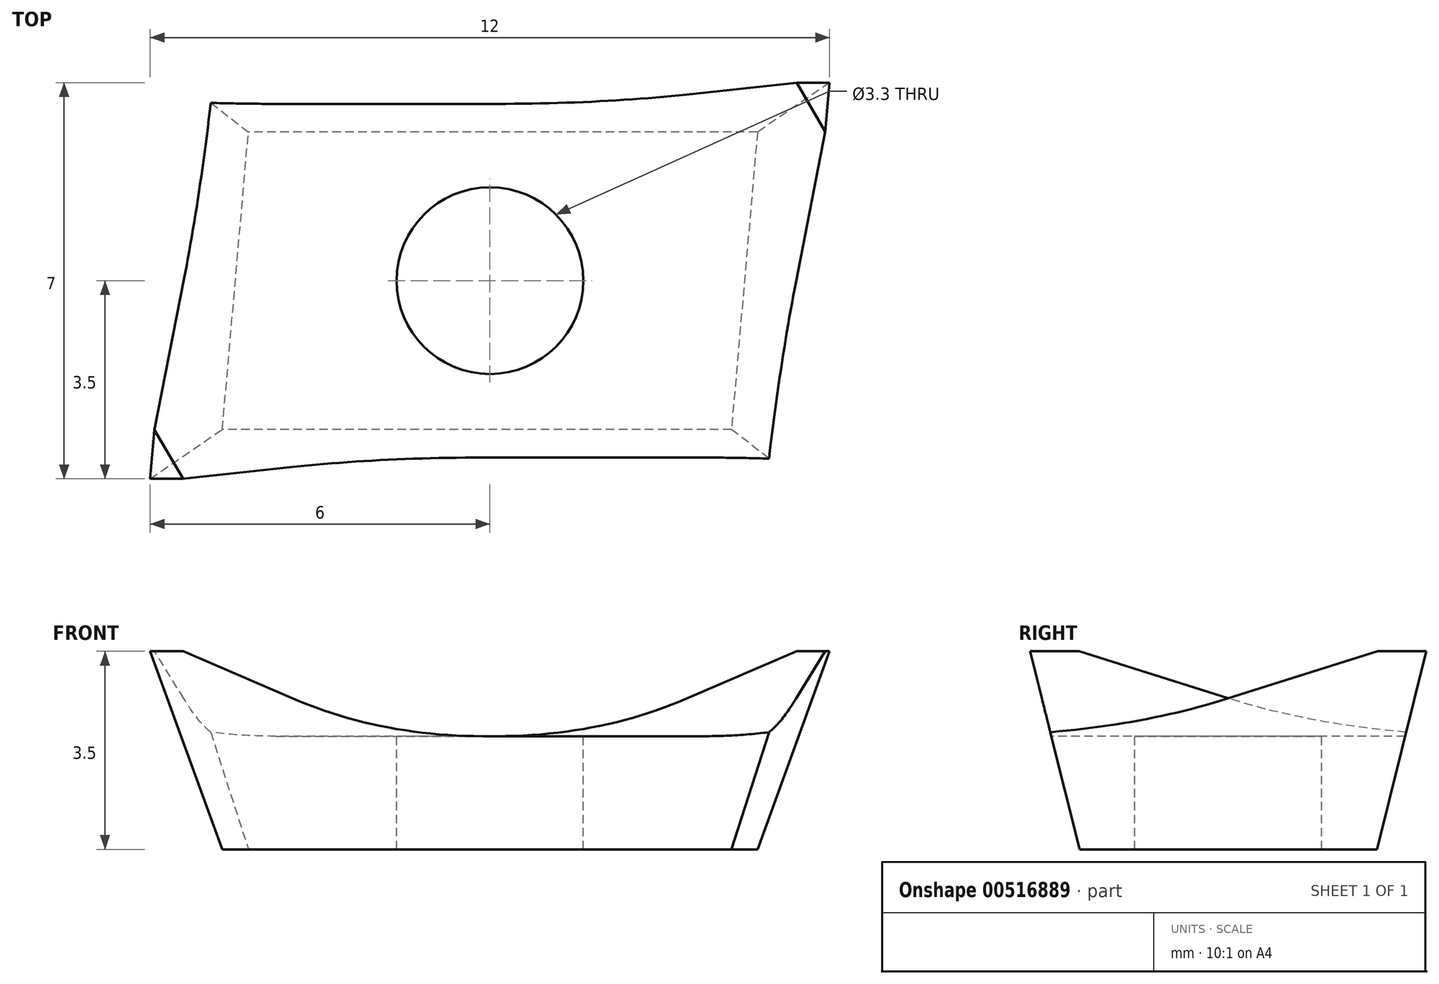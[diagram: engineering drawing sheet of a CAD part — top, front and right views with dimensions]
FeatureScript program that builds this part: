
annotation { "Feature Type Name" : "Feature", "Feature Type Description" : "" }
export const myFeature = defineFeature(function(context is Context, id is Id, definition is map)
    precondition{}
    {
        {
            var Q0;
            Q0=qCreatedBy(makeId("Top.planeOp"),FACE);
            var sketch = newSketch(context, id + "F0", { "sketchPlane" : qUnion([Q0])});
            skLineSegment(sketch, "E0.bottom", {"start": v(0, 0) * mm, "end": v(12, 0) * mm});
            skLineSegment(sketch, "E0.top", {"start": v(0, 7) * mm, "end": v(12, 7) * mm});
            skLineSegment(sketch, "E0.left", {"start": v(0, 0) * mm, "end": v(0, 7) * mm});
            skLineSegment(sketch, "E0.right", {"start": v(12, 0) * mm, "end": v(12, 7) * mm});
            skSolve(sketch);
        }
        {
            var Q0;
            Q0 = qSketchRegion(id + "F0", true);
            extrude(context, id + "F1", {"entities" : qUnion([Q0]), "depth" : 3.5 * mm, "offsetDistance" : 25 * mm});
        }
        {
            var Q0;
            Q0=makeQuery(id+"F1.opExtrude","SWEPT_FACE",FACE,{"disambiguationData":[OSD([sQuery(id+"F0.wireOp",EDGE,"E0.bottom")])]});
            var sketch = newSketch(context, id + "F2", { "sketchPlane" : qUnion([Q0])});
            skLineSegment(sketch, "E1", {"start": v(0, 3.5) * mm, "end": v(1.27, 0) * mm});
            skLineSegment(sketch, "E2", {"start": v(12, 3.5) * mm, "end": v(10.73, 0) * mm});
            skSolve(sketch);
        }
        {
            var Q0;
            {var subQ0=sQuery(id+"F2.wireOp",EDGE,"E1");Q0=makeQuery(id+"F2.imprint","IMPRINT",FACE,{"disambiguationData":[TD([[makeQuery(id+"F2.imprint","IMPRINT",EDGE,{"derivedFrom":subQ0}),-1.0]])]});}
            var Q1;
            {var subQ0=sQuery(id+"F2.wireOp",EDGE,"E2");Q1=makeQuery(id+"F2.imprint","IMPRINT",FACE,{"disambiguationData":[TD([[makeQuery(id+"F2.imprint","IMPRINT",EDGE,{"derivedFrom":subQ0}),1.0]])]});}
            extrude(context, id + "F3", {"entities" : qUnion([Q0, Q1]), "operationType" : NewBodyOperationType.REMOVE, "endBound" : BoundingType.THROUGH_ALL, "oppositeDirection" : true, "depth" : 25 * mm, "offsetDistance" : 25 * mm});
        }
        {
            var Q0;
            Q0=qCreatedBy(makeId("Right.planeOp"),FACE);
            var sketch = newSketch(context, id + "F4", { "sketchPlane" : qUnion([Q0])});
            skLineSegment(sketch, "E3.0.0", {"start": v(7, 0) * mm, "end": v(7, 3.5) * mm});
            skLineSegment(sketch, "E3.0.1", {"start": v(7, 3.5) * mm, "end": v(0, 3.5) * mm});
            skLineSegment(sketch, "E3.0.2", {"start": v(0, 3.5) * mm, "end": v(0, 0) * mm});
            skLineSegment(sketch, "E3.0.3", {"start": v(0, 0) * mm, "end": v(7, 0) * mm});
            skLineSegment(sketch, "E4", {"start": v(0, 3.5) * mm, "end": v(0.87, 0) * mm});
            skLineSegment(sketch, "E5", {"start": v(7, 3.5) * mm, "end": v(6.13, 0) * mm});
            skSolve(sketch);
        }
        {
            var Q0;
            {var subQ0=sQuery(id+"F4.wireOp",EDGE,"E3.0.2");Q0=makeQuery(id+"F4.imprint","IMPRINT",FACE,{"disambiguationData":[TD([[makeQuery(id+"F4.imprint","IMPRINT",EDGE,{"derivedFrom":subQ0}),1.0]])]});}
            var Q1;
            {var subQ0=sQuery(id+"F4.wireOp",EDGE,"E3.0.0");Q1=makeQuery(id+"F4.imprint","IMPRINT",FACE,{"disambiguationData":[TD([[makeQuery(id+"F4.imprint","IMPRINT",EDGE,{"derivedFrom":subQ0}),1.0]])]});}
            extrude(context, id + "F5", {"entities" : qUnion([Q0, Q1]), "operationType" : NewBodyOperationType.REMOVE, "endBound" : BoundingType.THROUGH_ALL, "depth" : 25 * mm, "offsetDistance" : 25 * mm});
        }
        {
            var Q0;
            Q0=makeQuery(id+"F1.opExtrude","CAP_FACE",FACE,{"disambiguationData":[OSD([sQuery(id+"F0.wireOp",EDGE,"E0.bottom"),sQuery(id+"F0.wireOp",EDGE,"E0.top"),sQuery(id+"F0.wireOp",EDGE,"E0.left"),sQuery(id+"F0.wireOp",EDGE,"E0.right")])],"isStart":false});
            var sketch = newSketch(context, id + "F6", { "sketchPlane" : qUnion([Q0])});
            skLineSegment(sketch, "E6", {"start": v(0, 0) * mm, "end": v(0.61, 7) * mm});
            skLineSegment(sketch, "E7.0", {"start": v(0, 0) * mm, "end": v(0, 7) * mm});
            skLineSegment(sketch, "E8.0", {"start": v(0, 7) * mm, "end": v(0.61, 7) * mm});
            skPoint(sketch, "E9.orphan", {"position": v(12, 7) * mm});
            skLineSegment(sketch, "E10.0", {"start": v(12, 0) * mm, "end": v(12, 7) * mm});
            skLineSegment(sketch, "E11.0", {"start": v(11.39, 0) * mm, "end": v(12, 0) * mm});
            skLineSegment(sketch, "E12", {"start": v(12, 7) * mm, "end": v(11.39, 0) * mm});
            skSolve(sketch);
        }
        {
            var Q0;
            Q0=makeQuery(id+"F1.opExtrude","CAP_FACE",FACE,{"disambiguationData":[OSD([sQuery(id+"F0.wireOp",EDGE,"E0.bottom"),sQuery(id+"F0.wireOp",EDGE,"E0.top"),sQuery(id+"F0.wireOp",EDGE,"E0.left"),sQuery(id+"F0.wireOp",EDGE,"E0.right")])],"isStart":true});
            var sketch = newSketch(context, id + "F7", { "sketchPlane" : qUnion([Q0])});
            skLineSegment(sketch, "E13.0", {"start": v(1.27, -6.13) * mm, "end": v(1.27, -0.87) * mm});
            skLineSegment(sketch, "E14.0", {"start": v(1.73, -6.13) * mm, "end": v(1.27, -6.13) * mm});
            skLineSegment(sketch, "E15", {"start": v(1.27, -0.87) * mm, "end": v(1.73, -6.13) * mm});
            skPoint(sketch, "E16.orphan", {"position": v(10.73, -6.13) * mm});
            skLineSegment(sketch, "E17.0", {"start": v(10.73, -6.13) * mm, "end": v(10.73, -0.87) * mm});
            skLineSegment(sketch, "E18.0", {"start": v(10.73, -0.87) * mm, "end": v(10.27, -0.87) * mm});
            skLineSegment(sketch, "E19", {"start": v(10.73, -6.13) * mm, "end": v(10.27, -0.87) * mm});
            skSolve(sketch);
        }
        {
            var Q1;
            Q1=makeQuery(id+"F6.imprint","IMPRINT",FACE,{"disambiguationData":[TD([[makeQuery(id+"F6.imprint","IMPRINT",EDGE,{"derivedFrom":sQuery(id+"F6.wireOp",EDGE,"E6")}),1.0]])]});
            var Q2;
            Q2=makeQuery(id+"F7.imprint","IMPRINT",FACE,{"disambiguationData":[TD([[makeQuery(id+"F7.imprint","IMPRINT",EDGE,{"derivedFrom":sQuery(id+"F7.wireOp",EDGE,"E13.0")}),-1.0]])]});
            loft(context, id + "F8", {"operationType" : NewBodyOperationType.REMOVE, "sheetProfilesArray" : [{ "sheetProfileEntities" : qUnion([Q1]) }, { "sheetProfileEntities" : qUnion([Q2]) }]});
        }
        {
            var Q1;
            Q1=makeQuery(id+"F6.imprint","IMPRINT",FACE,{"disambiguationData":[TD([[makeQuery(id+"F6.imprint","IMPRINT",EDGE,{"derivedFrom":sQuery(id+"F6.wireOp",EDGE,"E10.0")}),1.0]])]});
            var Q2;
            Q2=makeQuery(id+"F7.imprint","IMPRINT",FACE,{"disambiguationData":[TD([[makeQuery(id+"F7.imprint","IMPRINT",EDGE,{"derivedFrom":sQuery(id+"F7.wireOp",EDGE,"E17.0")}),1.0]])]});
            loft(context, id + "F9", {"operationType" : NewBodyOperationType.REMOVE, "sheetProfilesArray" : [{ "sheetProfileEntities" : qUnion([Q1]) }, { "sheetProfileEntities" : qUnion([Q2]) }]});
        }
        {
            var Q0;
            {var subQ0=sQuery(id+"F4.wireOp",EDGE,"E4");var subQ1=sQuery(id+"F4.wireOp",EDGE,"E3.0.2");var subQ2=sQuery(id+"F4.wireOp",EDGE,"E3.0.1");var subQ3=sQuery(id+"F0.wireOp",EDGE,"E0.bottom");var subQ4=sQuery(id+"F0.wireOp",EDGE,"E0.left");Q0=makeQuery(id+"F8.boolean.opBoolean","MERGE",VERTEX,{"derivedFrom":[makeQuery(id+"F5.boolean.opBoolean","MERGE",VERTEX,{"derivedFrom":[makeQuery(id+"F3.boolean.opBoolean","MERGE",VERTEX,{"derivedFrom":[makeQuery(id+"F1.opExtrude","CAP_VERTEX",VERTEX,{"disambiguationData":[OSD([subQ3,subQ4])],"isStart":false}),makeQuery(id+"F3.opExtrude","CAP_VERTEX",VERTEX,{"disambiguationData":[OSD([subQ3,subQ4,sQuery(id+"F2.wireOp",EDGE,"E1")])],"isStart":true})]}),makeQuery(id+"F5.opExtrude","CAP_VERTEX",VERTEX,{"disambiguationData":[OSD([subQ2,subQ1,subQ0])],"isStart":true})]}),makeQuery(id+"F8.opLoft","MID_CAP_VERTEX",VERTEX,{"disambiguationData":[OSD([subQ3,subQ2,subQ1,subQ0,sQuery(id+"F6.wireOp",EDGE,"E6"),sQuery(id+"F6.wireOp",EDGE,"E7.0")])],"capPos":0.0})]});}
            var Q1;
            {var subQ0=sQuery(id+"F0.wireOp",EDGE,"E0.top");Q1=makeQuery(id+"F9.boolean.opBoolean","MERGE",VERTEX,{"derivedFrom":[makeQuery(id+"F1.opExtrude","CAP_VERTEX",VERTEX,{"disambiguationData":[OSD([subQ0,sQuery(id+"F0.wireOp",EDGE,"E0.right")])],"isStart":false}),makeQuery(id+"F9.opLoft","MID_CAP_VERTEX",VERTEX,{"disambiguationData":[OSD([subQ0,sQuery(id+"F4.wireOp",EDGE,"E3.0.0"),sQuery(id+"F4.wireOp",EDGE,"E3.0.1"),sQuery(id+"F4.wireOp",EDGE,"E5"),sQuery(id+"F6.wireOp",EDGE,"E10.0"),sQuery(id+"F6.wireOp",EDGE,"E12")])],"capPos":0.0})]});}
            var Q2;
            Q2=qCreatedBy(makeId("Origin.pointOp"),VERTEX);
            cPlane(context, id + "F10", {"entities" : qUnion([Q0, Q1, Q2]), "cplaneType" : CPlaneType.THREE_POINT, "offset" : 25 * mm, "width" : 150 * mm, "height" : 150 * mm});
        }
        {
            var Q0;
            Q0=qCreatedBy(id+"F10.planeOp",FACE);
            var sketch = newSketch(context, id + "F11", { "sketchPlane" : qUnion([Q0])});
            skLineSegment(sketch, "E20.0", {"start": v(0, 3.5) * mm, "end": v(9.84, 3.5) * mm});
            skLineSegment(sketch, "E21.0", {"start": v(9.84, 3.5) * mm, "end": v(13.9, 3.5) * mm});
            skLineSegment(sketch, "E22", {"start": v(6.95, 4.41) * mm, "end": v(6.95, -1.55) * mm, "construction": true});
            skLineSegment(sketch, "E23", {"start": v(0.5, 3.5) * mm, "end": v(3.7, 2) * mm});
            skLineSegment(sketch, "E24", {"start": v(3.7, 2) * mm, "end": v(6.95, 2) * mm});
            skLineSegment(sketch, "E25.MirrorCS", {"start": v(10.2, 2) * mm, "end": v(6.95, 2) * mm});
            skLineSegment(sketch, "E26.MirrorCS", {"start": v(13.4, 3.5) * mm, "end": v(10.2, 2) * mm});
            skSolve(sketch);
        }
        {
            var Q0;
            Q0 = qSketchRegion(id + "F11", true);
            extrude(context, id + "F12", {"entities" : qUnion([Q0]), "operationType" : NewBodyOperationType.REMOVE, "oppositeDirection" : true, "depth" : 25 * mm, "offsetDistance" : 25 * mm, "symmetric" : true});
        }
        {
            var Q0;
            Q0=makeQuery(id+"F12.boolean.opBoolean","COPY",FACE,{"derivedFrom":makeQuery(id+"F12.opExtrude","SWEPT_FACE",FACE,{"disambiguationData":[OSD([sQuery(id+"F11.wireOp",EDGE,"E24"),sQuery(id+"F11.wireOp",EDGE,"E25.MirrorCS")])]})});
            var sketch = newSketch(context, id + "F13", { "sketchPlane" : qUnion([Q0])});
            skCircle(sketch, "E27", {"center": v(6, 3.5) * mm, "radius": 1.65 * mm});
            skLineSegment(sketch, "E28", {"start": v(6, 3.5) * mm, "end": v(8.75, 3.5) * mm, "construction": true});
            skLineSegment(sketch, "E29", {"start": v(6, 3.5) * mm, "end": v(4.8, 5.55) * mm, "construction": true});
            skSolve(sketch);
        }
        {
            var Q0;
            Q0 = qSketchRegion(id + "F13", true);
            extrude(context, id + "F14", {"entities" : qUnion([Q0]), "operationType" : NewBodyOperationType.REMOVE, "endBound" : BoundingType.THROUGH_ALL, "oppositeDirection" : true, "depth" : 25 * mm, "offsetDistance" : 25 * mm});
        }
        {
            var Q0;
            Q0=makeQuery(id+"F12.boolean.opBoolean","COPY",EDGE,{"derivedFrom":makeQuery(id+"F12.opExtrude","SWEPT_EDGE",EDGE,{"disambiguationData":[OSD([sQuery(id+"F11.wireOp",EDGE,"E23"),sQuery(id+"F11.wireOp",EDGE,"E24")])]})});
            var Q1;
            Q1=makeQuery(id+"F12.boolean.opBoolean","COPY",EDGE,{"derivedFrom":makeQuery(id+"F12.opExtrude","SWEPT_EDGE",EDGE,{"disambiguationData":[OSD([sQuery(id+"F11.wireOp",EDGE,"E25.MirrorCS"),sQuery(id+"F11.wireOp",EDGE,"E26.MirrorCS")])]})});
            fillet(context, id + "F15", {"entities" : qUnion([Q0, Q1]), "radius" : 7 * mm, "tangentPropagation" : true, "allowEdgeOverflow" : false});
        }
    });
